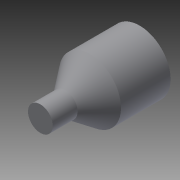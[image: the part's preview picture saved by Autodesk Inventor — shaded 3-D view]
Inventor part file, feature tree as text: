
AUTODESK INVENTOR PART (.ipt)
format: ipt  version: 2014 SP1 (Build 180222100, 222)  size: 153,088 bytes
history: native  units: in
note: dims shown in document units (in); Inventor stores cm internally (conversion verified against a paired STEP export)
features: extrude x4, sketch x3, pattern_circular x1, revolve x1, projected_geometry x1
ambient origin geometry x8: Origin, YZ Plane, XZ Plane, XY Plane, X Axis, Y Axis, Z Axis, Center Point
bodies: Solid1 (feature_tree)
feature tree (10):
  sketch  "Sketch1"  dims[d0=1.25in d2=60.0deg d3=0.1575in d4=0.7874in]
  extrude  "Extrusion1"  Depth=0.1575in TaperAngle=60.0deg
  extrude  "Extrusion2"  Depth=2.3622in TaperAngle=360.0deg
  extrude  "Extrusion3"  Depth=0.6in TaperAngle=0.0deg
  pattern_circular  "Circular Pattern1"  [2 undecoded]
  extrude  "Extrusion4"  Depth=0.25in TaperAngle=360.0deg
  revolve  "Revolution1"  [1 undecoded]
  sketch  "Sketch2"  dims[d5=0.6378in d6=2.3622in d8=360.0deg]
  sketch  "Sketch4"  dims[d10=1.0in d11=0.0in d12=0.6in d13=0.0in d14=0.6in d15=0.0in d16=2.3622in d17=360.0deg d19=0.375in d20=0.3in d21=0.0in d22=1.0in d23=0.25in d24=0.5in d25=90.0deg]
  projected_geometry  "Project Cut Edges1"
note: 3 required parameter values undecoded (feature->parameter linkage not recoverable at this tier; creation-order binding heuristic only, values carry confidence <= 0.55)